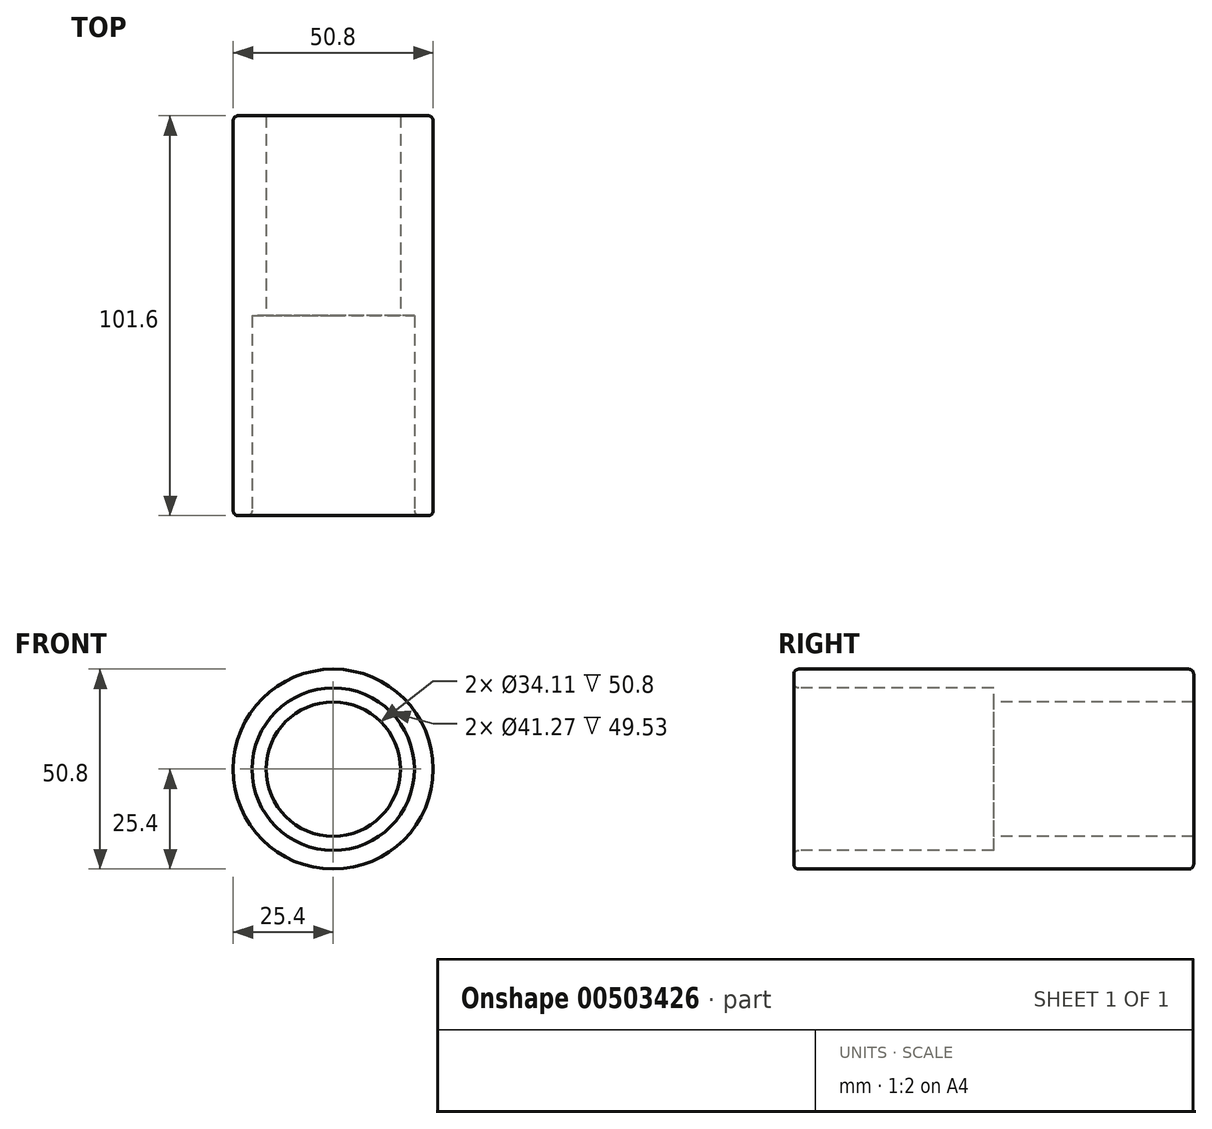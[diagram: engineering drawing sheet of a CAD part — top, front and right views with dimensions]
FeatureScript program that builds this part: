
annotation { "Feature Type Name" : "Feature", "Feature Type Description" : "" }
export const myFeature = defineFeature(function(context is Context, id is Id, definition is map)
    precondition{}
    {
        {
            var Q0;
            Q0=qCreatedBy(makeId("Front.planeOp"),FACE);
            var sketch = newSketch(context, id + "F0", { "sketchPlane" : qUnion([Q0])});
            skCircle(sketch, "E0", {"center": v(0, 0) * mm, "radius": 25.4 * mm});
            skSolve(sketch);
        }
        {
            var Q0;
            Q0=makeQuery(id+"F0.imprint","IMPRINT",FACE,{"disambiguationData":[TD([[makeQuery(id+"F0.imprint","IMPRINT",EDGE,{"derivedFrom":sQuery(id+"F0.wireOp",EDGE,"E0")}),1.0]])]});
            extrude(context, id + "F1", {"entities" : qUnion([Q0]), "depth" : 101.6 * mm});
        }
        {
            var Q0;
            Q0=makeQuery(id+"F1.opExtrude","CAP_FACE",FACE,{"disambiguationData":[OSD([sQuery(id+"F0.wireOp",EDGE,"E0")])],"isStart":false});
            cPlane(context, id + "F2", {"entities" : qUnion([Q0]), "cplaneType" : CPlaneType.OFFSET, "offset" : 0 * mm, "width" : 152.4 * mm, "height" : 152.4 * mm});
        }
        {
            var Q0;
            Q0=qCreatedBy(id+"F2.planeOp",FACE);
            var sketch = newSketch(context, id + "F3", { "sketchPlane" : qUnion([Q0])});
            skPoint(sketch, "E1", {"position": v(0, 0) * mm});
            skCircle(sketch, "E2", {"center": v(0, 0) * mm, "radius": 20.64 * mm});
            skSolve(sketch);
        }
        {
            var Q0;
            Q0=sQuery(id+"F3.wireOp",VERTEX,"E1");
            var Q1;
            Q1=makeQuery(id+"F1.opExtrude","SWEPT_BODY",BODY,{"disambiguationData":[OSD([sQuery(id+"F0.wireOp",EDGE,"E0")])]});
            hole(context, id + "F4", {"style" : HoleStyle.SIMPLE, "endStyle" : HoleEndStyle.THROUGH, "holeDiameter" : 34.1 * mm, "isTappedThrough" : true, "tappedDepth" : 12.7 * mm, "tapClearance" : 3, "locations" : qUnion([Q0]), "scope" : qUnion([Q1])});
        }
        {
            var Q0;
            Q0=makeQuery(id+"F3.imprint","IMPRINT",FACE,{"disambiguationData":[TD([[makeQuery(id+"F3.imprint","IMPRINT",EDGE,{"derivedFrom":sQuery(id+"F3.wireOp",EDGE,"E2")}),1.0]])]});
            extrude(context, id + "F5", {"entities" : qUnion([Q0]), "operationType" : NewBodyOperationType.REMOVE, "oppositeDirection" : true, "depth" : 50.8 * mm});
        }
        {
            var Q0;
            Q0=makeQuery(id+"F1.opExtrude","SWEPT_FACE",FACE,{"disambiguationData":[OSD([sQuery(id+"F0.wireOp",EDGE,"E0")])]});
            var Q1;
            Q1=makeQuery(id+"F1.opExtrude","CAP_FACE",FACE,{"disambiguationData":[OSD([sQuery(id+"F0.wireOp",EDGE,"E0")])],"isStart":false});
            var Q2;
            Q2=makeQuery(id+"F4.hole-0.boolean.opBoolean","COPY",FACE,{"derivedFrom":makeQuery(id+"F4.hole-0.opRevolve","SWEPT_FACE",FACE,{"disambiguationData":[OSD([sQuery(id+"F4.hole-0.sketch.wireOp",EDGE,"core_line_2")])]})});
            fillet(context, id + "F6", {"entities" : qUnion([Q0, Q1, Q2]), "radius" : 1.27 * mm, "tangentPropagation" : true, "allowEdgeOverflow" : false});
        }
    });
